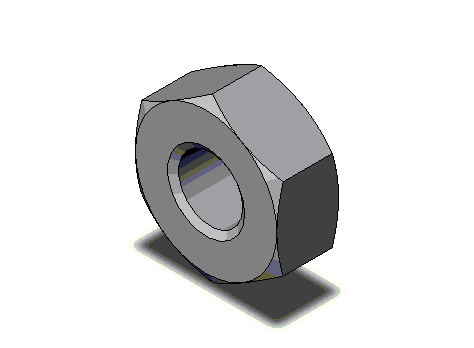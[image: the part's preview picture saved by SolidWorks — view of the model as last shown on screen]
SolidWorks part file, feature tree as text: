
SOLIDWORKS PART (.sldprt)
format: sldprt  version: not decoded by parser v0  size: 252,928 bytes
history: native  units: mm
features: sketch x5, cut_revolve x4, plane x3, material x1, extrude x1, thread x1, pattern_linear x1 (+11 scaffold rows collapsed; 1 parser-record rows omitted)
feature tree (28):
  parser-record x1  (decoder bookkeeping rows leaked as tree rows — omitted from the tree; the rows remain in map.json)
  scaffold x11  (default folders/planes/origin — collapsed)
  material  "Material <not specified>"
  plane  "Plane1"
  plane  "Plane2"
  plane  "Plane3"
  sketch  "BaseNutSke"  dims[c1.Tap_drill=2.5mm c1.D1=50.8mm c2.D1=30.0deg c2.D2=~24.797543mm c3.D2=60.0deg c3.D3=50.8mm c4.D3=30.0deg c4.D4=~24.797543mm c5.D4=60.0deg c6.D4=~24.797543mm c7.D4=60.0deg c8.D4=~24.797543mm c9.D4=60.0deg c9.Width_flats=5.5mm c9.D1=~21.475302mm c9.D2=~21.475302mm c10.D1=~21.475302mm c10.D2=2.75mm c10.D3=2.75mm c11.D1=~24.797543mm c12.D1=120.0deg c13.D1=~23.397294mm c14.D1=120.0deg c14.D4=2.75mm]
  extrude  "BaseNut"  [1 undecoded]
  thread  "ThreadCosmetic"  [2 undecoded]
  cut_revolve  "EndChamfer"  [1 undecoded]
  sketch  "Sketch5"
  pattern_linear  "ThdSchPat"  [2 undecoded]
  cut_revolve  "ThreadSchematic"  [1 undecoded]
  sketch  "ThdSchSke"  dims[c1.D1=~4.490128mm c2.D1=90.0deg c3.D1=~4.490128mm c3.VeeAngle=70.0deg c4.D1=19.5834mm c4.SideAngle=55.0deg c5.D1=~4.490128mm c5.SideAngle=55.0deg c5.ThreadDepth=2.54mm c6.ThreadDepth=3.175mm c6.Thread_Major=6.35mm c6.D1=~9.573347mm c6.D2=~9.428305mm c6.OverCut=1.25mm c6.Tap_Drill=2.5mm c6.Advance=1.27mm c6.Thread_major=3.0mm c7.Advance=0.5mm c7.D1=6.35mm c7.D2=0.0254mm c8.D1=0.0254mm c9.D1=360.0deg c9.Num_threads=6.0 c9.Advance=~0.46984mm c9.D2=1.0 c9.D4=50.0mm c10.D1=~8.980256mm c11.D1=315.0deg c12.D1=~8.980256mm c13.D1=45.0deg c13.D2=~8.94581mm c14.D2=~1.952549deg c14.D3=6.35mm c15.D2=25.7048mm c15.D1=~6.352235mm c16.D1=35.0deg c16.D2=12.7mm c16.D3=12.7mm c17.D2=22.5552mm c17.D3=25.4mm c17.D4=12.7mm c18.D3=12.7mm c18.D2=0.0508mm c18.Offset1=25.4254mm c18.ThreadMajor=12.7mm c18.ChamferDepth=0.275mm c18.Offset2=2.4762mm c19.ThreadMajor=1.5mm c19.Offset1=2.4254mm c19.D1=360.0deg c19.Thread_major=3.0mm c19.Thickness=2.4mm]
  sketch  "Sketch4"  dims[c1.D1=38.1mm c1.Bearing_ht=0.01mm c1.D3=12.7mm c1.D4=10.0mm c1.D5=2.54mm c1.D6=18.8722mm c2.D3=10.0mm c2.D1=2.75mm c2.D2=~3.890588mm c3.D2=~139.242599deg c4.D2=22.5298mm c5.D2=45.0deg c6.D2=~10.392305mm c7.D2=30.0deg]
  cut_revolve  "Bearing-Face"  Angle=360deg
  sketch  "Sketch3"  dims[c1.D1=2.75mm c1.D2=2.4mm c1.D3=12.7mm c1.D4=10.0mm c1.D5=10.9093mm c1.D6=~10.998523mm c2.D6=~179.413404deg c3.D6=~2.539714mm c3.D3=10.0mm c3.D5=9.525mm c3.D2=~10.392305mm c4.D2=30.0deg]
  cut_revolve  "Double-Chamfer"  Angle=360deg ConfigurationName=0mm CopiedFlag=1 PartNumberID=0mm
decode coverage: 6 of 12 modeling features carry decoded parameters
note: ~ marks probable driven/reference dimensions
note: 7 parameter values undecoded
summary: no parameter record found for 4 features
note: suppression state not decoded; provenance and decode notes live in map.json
